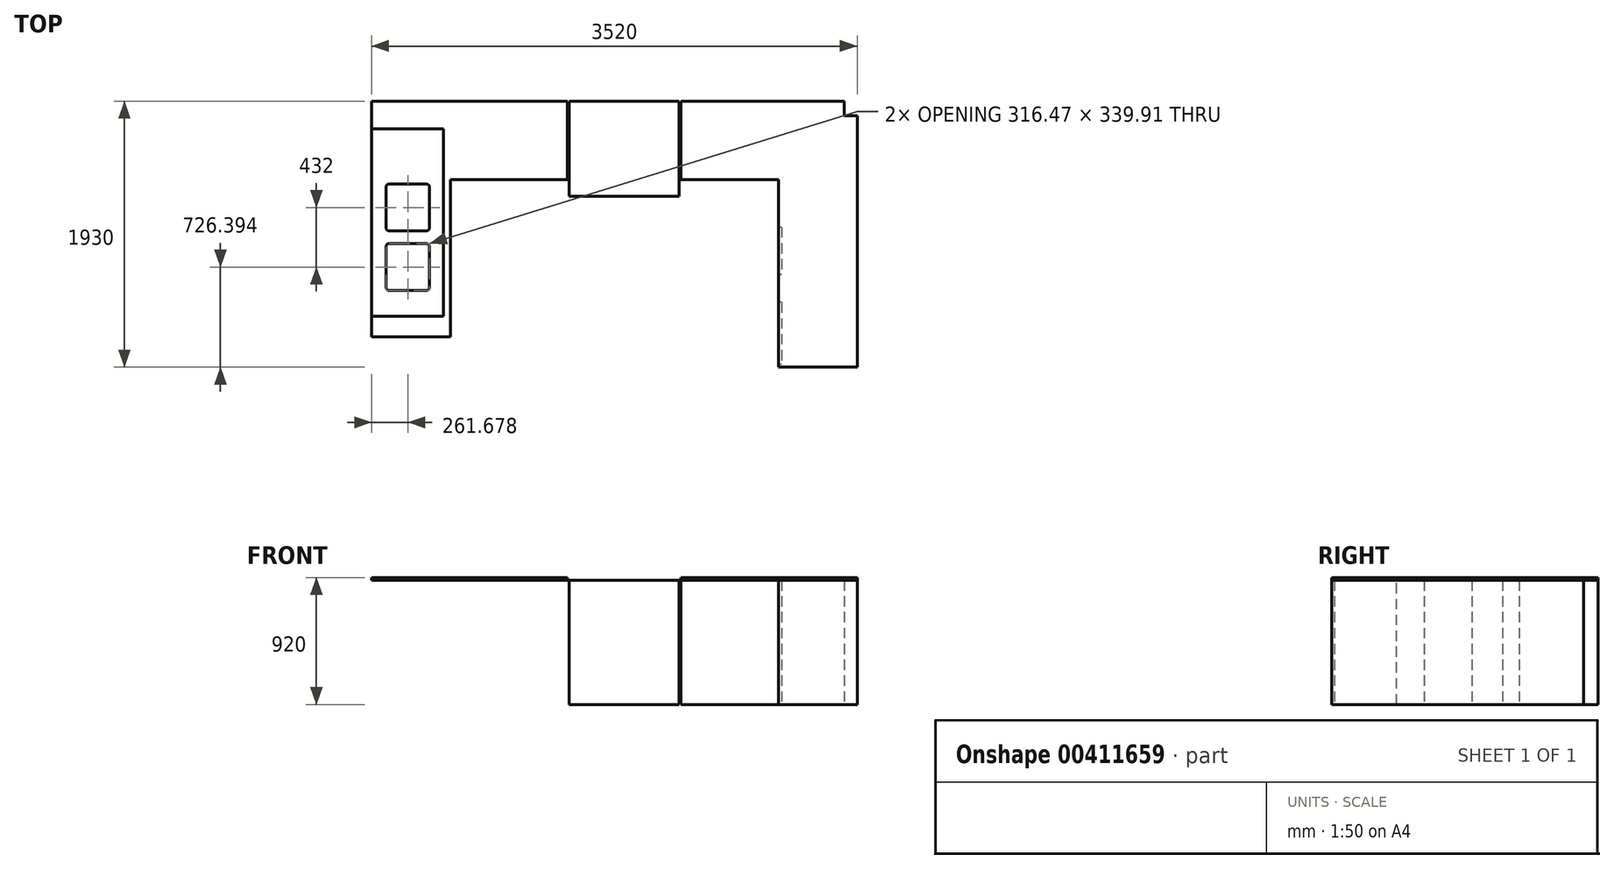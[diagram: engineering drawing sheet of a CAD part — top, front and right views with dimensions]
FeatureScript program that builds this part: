
annotation { "Feature Type Name" : "Feature", "Feature Type Description" : "" }
export const myFeature = defineFeature(function(context is Context, id is Id, definition is map)
    precondition{}
    {
        {
            var Q0;
            Q0=qCreatedBy(makeId("Top.planeOp"),FACE);
            var sketch = newSketch(context, id + "F0", { "sketchPlane" : qUnion([Q0])});
            skLineSegment(sketch, "E0.bottom", {"start": v(-1763.99, -609.92) * mm, "end": v(-1193.99, -609.92) * mm});
            skLineSegment(sketch, "E0.left", {"start": v(-1763.99, -609.92) * mm, "end": v(-1763.99, 1100.08) * mm});
            skLineSegment(sketch, "E0.right", {"start": v(-1193.99, -609.92) * mm, "end": v(-1193.99, 530.08) * mm});
            skLineSegment(sketch, "E1.bottom", {"start": v(-1763.99, 1100.08) * mm, "end": v(1661.01, 1100.08) * mm});
            skLineSegment(sketch, "E1.top", {"start": v(-1193.99, 530.08) * mm, "end": v(-343.99, 530.08) * mm});
            skLineSegment(sketch, "E2.top", {"start": v(1756.01, -829.92) * mm, "end": v(1186.01, -829.92) * mm});
            skLineSegment(sketch, "E2.left", {"start": v(1756.01, 995.08) * mm, "end": v(1756.01, -829.92) * mm});
            skLineSegment(sketch, "E2.right", {"start": v(1186.01, 530.08) * mm, "end": v(1186.01, -829.92) * mm});
            skLineSegment(sketch, "E3.bottom", {"start": v(-343.99, 1100.08) * mm, "end": v(476.01, 1100.08) * mm});
            skLineSegment(sketch, "E3.top", {"start": v(-331.49, 409.53) * mm, "end": v(463.51, 409.53) * mm});
            skLineSegment(sketch, "E3.left", {"start": v(-343.99, 1100.08) * mm, "end": v(-343.99, 530.08) * mm});
            skLineSegment(sketch, "E3.right", {"start": v(476.01, 1100.08) * mm, "end": v(476.01, 530.08) * mm});
            skLineSegment(sketch, "E4.trimOffspring", {"start": v(476.01, 530.08) * mm, "end": v(1186.01, 530.08) * mm});
            skLineSegment(sketch, "E5.top", {"start": v(1756.01, 995.08) * mm, "end": v(1661.01, 995.08) * mm});
            skLineSegment(sketch, "E5.right", {"start": v(1661.01, 1100.08) * mm, "end": v(1661.01, 995.08) * mm});
            skLineSegment(sketch, "E6.bottom", {"start": v(-331.49, 1100.08) * mm, "end": v(463.51, 1100.08) * mm});
            skLineSegment(sketch, "E6.left", {"start": v(-331.49, 1100.08) * mm, "end": v(-331.49, 409.53) * mm});
            skLineSegment(sketch, "E6.right", {"start": v(463.51, 1100.08) * mm, "end": v(463.51, 409.53) * mm});
            skSolve(sketch);
        }
        {
            var Q0;
            Q0=makeQuery(id+"F0.imprint","IMPRINT",FACE,{"disambiguationData":[TD([[makeQuery(id+"F0.imprint","IMPRINT",EDGE,{"derivedFrom":sQuery(id+"F0.wireOp",EDGE,"E0.bottom")}),1.0]])]});
            var Q1;
            Q1=makeQuery(id+"F0.imprint","IMPRINT",FACE,{"disambiguationData":[TD([[makeQuery(id+"F0.imprint","IMPRINT",EDGE,{"derivedFrom":sQuery(id+"F0.wireOp",EDGE,"E2.top")}),-1.0]])]});
            extrude(context, id + "F1", {"entities" : qUnion([Q0, Q1]), "depth" : 900 * mm});
        }
        {
            var Q0;
            Q0 = qSketchRegion(id + "F0", true);
            extrude(context, id + "F2", {"entities" : qUnion([Q0]), "depth" : 900 * mm});
        }
        {
            var Q0;
            Q0=makeQuery(id+"F1.opExtrude","CAP_FACE",FACE,{"disambiguationData":[OSD([sQuery(id+"F0.wireOp",EDGE,"E0.bottom"),sQuery(id+"F0.wireOp",EDGE,"E0.left"),sQuery(id+"F0.wireOp",EDGE,"E0.right"),sQuery(id+"F0.wireOp",EDGE,"E1.bottom"),sQuery(id+"F0.wireOp",EDGE,"E1.top"),sQuery(id+"F0.wireOp",EDGE,"E3.left")])],"isStart":false});
            var Q1;
            Q1=makeQuery(id+"F1.opExtrude","CAP_FACE",FACE,{"disambiguationData":[OSD([sQuery(id+"F0.wireOp",EDGE,"E1.bottom"),sQuery(id+"F0.wireOp",EDGE,"E2.top"),sQuery(id+"F0.wireOp",EDGE,"E2.left"),sQuery(id+"F0.wireOp",EDGE,"E2.right"),sQuery(id+"F0.wireOp",EDGE,"E3.right"),sQuery(id+"F0.wireOp",EDGE,"E4.trimOffspring"),sQuery(id+"F0.wireOp",EDGE,"E5.top"),sQuery(id+"F0.wireOp",EDGE,"E5.right")])],"isStart":false});
            extrude(context, id + "F3", {"entities" : qUnion([Q0, Q1]), "depth" : 20 * mm});
        }
        {
            var Q0;
            Q0=makeQuery(id+"F3.opExtrude","CAP_FACE",FACE,{"disambiguationData":[OSD([sQuery(id+"F0.wireOp",EDGE,"E0.bottom"),sQuery(id+"F0.wireOp",EDGE,"E0.left"),sQuery(id+"F0.wireOp",EDGE,"E0.right"),sQuery(id+"F0.wireOp",EDGE,"E1.bottom"),sQuery(id+"F0.wireOp",EDGE,"E1.top"),sQuery(id+"F0.wireOp",EDGE,"E3.left")])],"isStart":false});
            var sketch = newSketch(context, id + "F4", { "sketchPlane" : qUnion([Q0])});
            skLineSegment(sketch, "E7.bottom", {"start": v(-1763.99, 900.08) * mm, "end": v(-1243.99, 900.08) * mm});
            skLineSegment(sketch, "E7.top", {"start": v(-1763.99, -459.92) * mm, "end": v(-1243.99, -459.92) * mm});
            skLineSegment(sketch, "E7.left", {"start": v(-1763.99, 900.08) * mm, "end": v(-1763.99, -459.92) * mm});
            skLineSegment(sketch, "E7.right", {"start": v(-1243.99, 900.08) * mm, "end": v(-1243.99, -459.92) * mm});
            skLineSegment(sketch, "E8.bottom", {"start": v(-1660.54, 498.43) * mm, "end": v(-1344.08, 498.43) * mm});
            skLineSegment(sketch, "E8.top", {"start": v(-1660.54, 158.52) * mm, "end": v(-1344.08, 158.52) * mm});
            skLineSegment(sketch, "E8.left", {"start": v(-1660.54, 498.43) * mm, "end": v(-1660.54, 158.52) * mm});
            skLineSegment(sketch, "E8.right", {"start": v(-1344.08, 498.43) * mm, "end": v(-1344.08, 158.52) * mm});
            skLineSegment(sketch, "E9.bottom", {"start": v(-1660.54, 66.43) * mm, "end": v(-1344.08, 66.43) * mm});
            skLineSegment(sketch, "E9.top", {"start": v(-1660.54, -273.48) * mm, "end": v(-1344.08, -273.48) * mm});
            skLineSegment(sketch, "E9.left", {"start": v(-1660.54, 66.43) * mm, "end": v(-1660.54, -273.48) * mm});
            skLineSegment(sketch, "E9.right", {"start": v(-1344.08, 66.43) * mm, "end": v(-1344.08, -273.48) * mm});
            skSolve(sketch);
        }
        {
            var Q0;
            Q0=makeQuery(id+"F4.imprint","IMPRINT",FACE,{"disambiguationData":[TD([[makeQuery(id+"F4.imprint","IMPRINT",EDGE,{"derivedFrom":sQuery(id+"F4.wireOp",EDGE,"E9.bottom")}),-1.0]])]});
            var Q1;
            Q1=makeQuery(id+"F4.imprint","IMPRINT",FACE,{"disambiguationData":[TD([[makeQuery(id+"F4.imprint","IMPRINT",EDGE,{"derivedFrom":sQuery(id+"F4.wireOp",EDGE,"E8.bottom")}),-1.0]])]});
            var Q2;
            Q2=makeQuery(id+"F1.opExtrude","SWEPT_BODY",BODY,{"disambiguationData":[OSD([sQuery(id+"F0.wireOp",EDGE,"E0.bottom"),sQuery(id+"F0.wireOp",EDGE,"E0.left"),sQuery(id+"F0.wireOp",EDGE,"E0.right"),sQuery(id+"F0.wireOp",EDGE,"E1.bottom"),sQuery(id+"F0.wireOp",EDGE,"E1.top"),sQuery(id+"F0.wireOp",EDGE,"E3.left")])]});
            extrude(context, id + "F5", {"entities" : qUnion([Q0, Q1]), "operationType" : NewBodyOperationType.REMOVE, "endBound" : BoundingType.UP_TO_BODY, "oppositeDirection" : true, "endBoundEntityBody" : qUnion([Q2]), "depth" : 100 * mm});
        }
        {
            var Q0;
            Q0=makeQuery(id+"F4.imprint","IMPRINT",FACE,{"disambiguationData":[TD([[makeQuery(id+"F4.imprint","IMPRINT",EDGE,{"derivedFrom":sQuery(id+"F4.wireOp",EDGE,"E7.bottom")}),-1.0]])]});
            extrude(context, id + "F6", {"entities" : qUnion([Q0]), "operationType" : NewBodyOperationType.REMOVE, "oppositeDirection" : true, "depth" : 5 * mm});
        }
        {
            var Q0;
            Q0=makeQuery(id+"F5.boolean.opBoolean","COPY",EDGE,{"derivedFrom":makeQuery(id+"F5.opExtrude","SWEPT_EDGE",EDGE,{"disambiguationData":[OSD([sQuery(id+"F4.wireOp",EDGE,"E8.top"),sQuery(id+"F4.wireOp",EDGE,"E8.right")])]})});
            var Q1;
            Q1=makeQuery(id+"F5.boolean.opBoolean","COPY",EDGE,{"derivedFrom":makeQuery(id+"F5.opExtrude","SWEPT_EDGE",EDGE,{"disambiguationData":[OSD([sQuery(id+"F4.wireOp",EDGE,"E9.top"),sQuery(id+"F4.wireOp",EDGE,"E9.right")])]})});
            var Q2;
            Q2=makeQuery(id+"F5.boolean.opBoolean","COPY",EDGE,{"derivedFrom":makeQuery(id+"F5.opExtrude","SWEPT_EDGE",EDGE,{"disambiguationData":[OSD([sQuery(id+"F4.wireOp",EDGE,"E9.top"),sQuery(id+"F4.wireOp",EDGE,"E9.left")])]})});
            var Q3;
            Q3=makeQuery(id+"F5.boolean.opBoolean","COPY",EDGE,{"derivedFrom":makeQuery(id+"F5.opExtrude","SWEPT_EDGE",EDGE,{"disambiguationData":[OSD([sQuery(id+"F4.wireOp",EDGE,"E8.top"),sQuery(id+"F4.wireOp",EDGE,"E8.left")])]})});
            var Q4;
            Q4=makeQuery(id+"F5.boolean.opBoolean","COPY",EDGE,{"derivedFrom":makeQuery(id+"F5.opExtrude","SWEPT_EDGE",EDGE,{"disambiguationData":[OSD([sQuery(id+"F4.wireOp",EDGE,"E9.bottom"),sQuery(id+"F4.wireOp",EDGE,"E9.left")])]})});
            var Q5;
            Q5=makeQuery(id+"F5.boolean.opBoolean","COPY",EDGE,{"derivedFrom":makeQuery(id+"F5.opExtrude","SWEPT_EDGE",EDGE,{"disambiguationData":[OSD([sQuery(id+"F4.wireOp",EDGE,"E8.bottom"),sQuery(id+"F4.wireOp",EDGE,"E8.left")])]})});
            var Q6;
            Q6=makeQuery(id+"F5.boolean.opBoolean","COPY",EDGE,{"derivedFrom":makeQuery(id+"F5.opExtrude","SWEPT_EDGE",EDGE,{"disambiguationData":[OSD([sQuery(id+"F4.wireOp",EDGE,"E8.bottom"),sQuery(id+"F4.wireOp",EDGE,"E8.right")])]})});
            var Q7;
            Q7=makeQuery(id+"F5.boolean.opBoolean","COPY",EDGE,{"derivedFrom":makeQuery(id+"F5.opExtrude","SWEPT_EDGE",EDGE,{"disambiguationData":[OSD([sQuery(id+"F4.wireOp",EDGE,"E9.bottom"),sQuery(id+"F4.wireOp",EDGE,"E9.right")])]})});
            fillet(context, id + "F7", {"entities" : qUnion([Q0, Q1, Q2, Q3, Q4, Q5, Q6, Q7]), "radius" : 25 * mm, "tangentPropagation" : true, "allowEdgeOverflow" : false});
        }
        {
            var Q0;
            Q0=makeQuery(id+"F2.opExtrude","CAP_FACE",FACE,{"disambiguationData":[OSD([sQuery(id+"F0.wireOp",EDGE,"E0.bottom"),sQuery(id+"F0.wireOp",EDGE,"E0.left"),sQuery(id+"F0.wireOp",EDGE,"E0.right"),sQuery(id+"F0.wireOp",EDGE,"E1.bottom"),sQuery(id+"F0.wireOp",EDGE,"E1.top"),sQuery(id+"F0.wireOp",EDGE,"E3.left")])],"isStart":false});
            extrude(context, id + "F8", {"entities" : qUnion([Q0]), "operationType" : NewBodyOperationType.REMOVE, "endBound" : BoundingType.THROUGH_ALL, "oppositeDirection" : true, "depth" : 25 * mm});
        }
        {
            var Q0;
            Q0=makeQuery(id+"F1.opExtrude","SWEPT_FACE",FACE,{"disambiguationData":[OSD([sQuery(id+"F0.wireOp",EDGE,"E2.right")])]});
            var sketch = newSketch(context, id + "F9", { "sketchPlane" : qUnion([Q0])});
            skLineSegment(sketch, "E10", {"start": v(809.92, 900) * mm, "end": v(809.92, 0) * mm});
            skLineSegment(sketch, "E11", {"start": v(809.92, 0) * mm, "end": v(359.92, 0) * mm});
            skLineSegment(sketch, "E12", {"start": v(359.92, 0) * mm, "end": v(359.92, 900) * mm});
            skLineSegment(sketch, "E13", {"start": v(359.92, 900) * mm, "end": v(159.92, 900) * mm});
            skLineSegment(sketch, "E14", {"start": v(159.92, 900) * mm, "end": v(159.92, 0) * mm});
            skLineSegment(sketch, "E15", {"start": v(-185.08, 900) * mm, "end": v(-185.08, 0) * mm});
            skSolve(sketch);
        }
        {
            var Q0;
            {var subQ0=sQuery(id+"F9.wireOp",EDGE,"E10");Q0=makeQuery(id+"F9.imprint","IMPRINT",FACE,{"disambiguationData":[TD([[makeQuery(id+"F9.imprint","IMPRINT",EDGE,{"derivedFrom":subQ0}),-1.0]])]});}
            var Q1;
            {var subQ0=sQuery(id+"F9.wireOp",EDGE,"E14");Q1=makeQuery(id+"F9.imprint","IMPRINT",FACE,{"disambiguationData":[TD([[makeQuery(id+"F9.imprint","IMPRINT",EDGE,{"derivedFrom":subQ0}),-1.0]])]});}
            extrude(context, id + "F10", {"entities" : qUnion([Q0, Q1]), "operationType" : NewBodyOperationType.REMOVE, "oppositeDirection" : true, "depth" : 20 * mm});
        }
    });
